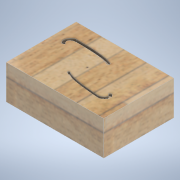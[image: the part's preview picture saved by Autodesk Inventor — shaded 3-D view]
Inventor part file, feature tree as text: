
AUTODESK INVENTOR PART (.ipt)
format: ipt  version: 2021 (Build 250183000, 183)  size: 401,920 bytes
history: native  units: in
note: dims shown in document units (in); Inventor stores cm internally (conversion verified against a paired STEP export)
features: sketch x8, extrude x7, plane x1
ambient origin geometry x8: Origin, YZ Plane, XZ Plane, XY Plane, X Axis, Y Axis, Z Axis, Center Point
bodies: Solid1 (feature_tree)
feature tree (16):
  extrude  "Extrusion1"  Depth=7.0in
  extrude  "Extrusion2"  Depth=0.2in
  extrude  "Extrusion3"  Depth=0.2in
  extrude  "Extrusion4"  Depth=0.2in
  extrude  "Extrusion5"  Depth=3.25in TaperAngle=0.0deg
  extrude  "Extrusion6"  Depth=3.25in TaperAngle=0.0deg
  sketch  "Sketch7"  dims[d17=0.25in d18=6.6in d19=0.0in]
  plane  "Work Plane1"
  extrude  "Extrusion9"  Depth=6.6in TaperAngle=0.0deg
  sketch  "Sketch1"  dims[d0=9.75in d1=7.0in]
  sketch  "Sketch2"  dims[d2=0.1875in d3=0.0in d4=0.2in]
  sketch  "Sketch3"  dims[d5=3.25in d6=0.0in d7=0.2in]
  sketch  "Sketch4"  dims[d8=3.25in d9=0.0in d10=0.2in]
  sketch  "Sketch5"  dims[d11=0.2in d12=3.25in d13=0.0in]
  sketch  "Sketch6"  dims[d14=0.2in d15=3.25in d16=0.0in]
  sketch  "Sketch10"  dims[d20=-0.0in d25=1.0in d26=0.0in d21=0.5in d22=0.0344in d23=0.5in d24=0.0344in]
